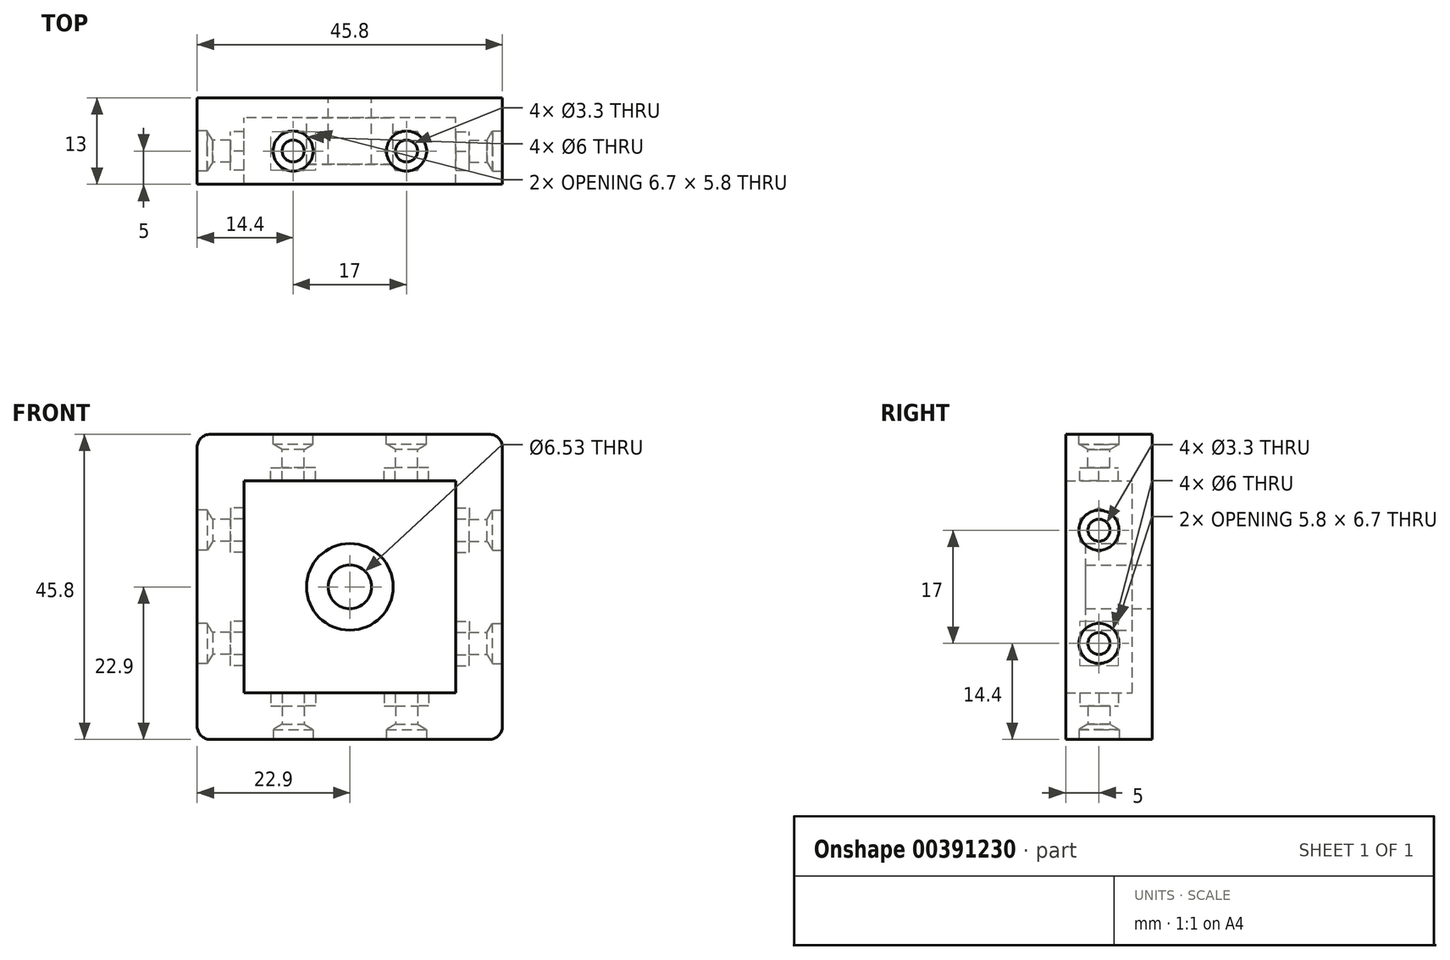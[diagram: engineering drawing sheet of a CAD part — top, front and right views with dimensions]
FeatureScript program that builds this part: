
annotation { "Feature Type Name" : "Feature", "Feature Type Description" : "" }
export const myFeature = defineFeature(function(context is Context, id is Id, definition is map)
    precondition{}
    {
        {
            var Q0;
            Q0=qCreatedBy(makeId("Front.planeOp"),FACE);
            var sketch = newSketch(context, id + "F0", { "sketchPlane" : qUnion([Q0])});
            skLineSegment(sketch, "E0.bottom", {"start": v(22.9, -22.9) * mm, "end": v(-22.9, -22.9) * mm});
            skLineSegment(sketch, "E0.top", {"start": v(22.9, 22.9) * mm, "end": v(-22.9, 22.9) * mm});
            skLineSegment(sketch, "E0.left", {"start": v(22.9, -22.9) * mm, "end": v(22.9, 22.9) * mm});
            skLineSegment(sketch, "E0.right", {"start": v(-22.9, -22.9) * mm, "end": v(-22.9, 22.9) * mm});
            skPoint(sketch, "E0.middle", {"position": v(0, 0) * mm});
            skLineSegment(sketch, "E1.bottom", {"start": v(15.9, -15.9) * mm, "end": v(-15.9, -15.9) * mm});
            skLineSegment(sketch, "E1.top", {"start": v(15.9, 15.9) * mm, "end": v(-15.9, 15.9) * mm});
            skLineSegment(sketch, "E1.left", {"start": v(15.9, -15.9) * mm, "end": v(15.9, 15.9) * mm});
            skLineSegment(sketch, "E1.right", {"start": v(-15.9, -15.9) * mm, "end": v(-15.9, 15.9) * mm});
            skCircle(sketch, "E2", {"center": v(0, 0) * mm, "radius": 6.5 * mm});
            skSolve(sketch);
        }
        {
            var Q0;
            Q0=makeQuery(id+"F0.imprint","IMPRINT",FACE,{"disambiguationData":[TD([[makeQuery(id+"F0.imprint","IMPRINT",EDGE,{"derivedFrom":sQuery(id+"F0.wireOp",EDGE,"E1.bottom")}),-1.0]])]});
            extrude(context, id + "F1", {"entities" : qUnion([Q0]), "depth" : 3 * mm});
        }
        {
            var Q0;
            Q0=makeQuery(id+"F0.imprint","IMPRINT",FACE,{"disambiguationData":[TD([[makeQuery(id+"F0.imprint","IMPRINT",EDGE,{"derivedFrom":sQuery(id+"F0.wireOp",EDGE,"E2")}),1.0]])]});
            extrude(context, id + "F2", {"entities" : qUnion([Q0]), "operationType" : NewBodyOperationType.ADD, "depth" : 10 * mm});
        }
        {
            var Q0;
            Q0=makeQuery(id+"F0.imprint","IMPRINT",FACE,{"disambiguationData":[TD([[makeQuery(id+"F0.imprint","IMPRINT",EDGE,{"derivedFrom":sQuery(id+"F0.wireOp",EDGE,"E0.bottom")}),-1.0]])]});
            extrude(context, id + "F3", {"entities" : qUnion([Q0]), "operationType" : NewBodyOperationType.ADD, "depth" : 13 * mm});
        }
        {
            var Q0;
            Q0=makeQuery(id+"F3.opExtrude","SWEPT_FACE",FACE,{"disambiguationData":[OSD([sQuery(id+"F0.wireOp",EDGE,"E0.bottom")])]});
            var sketch = newSketch(context, id + "F4", { "sketchPlane" : qUnion([Q0])});
            skPoint(sketch, "E3", {"position": v(-8.5, 8) * mm});
            skPoint(sketch, "E4", {"position": v(8.5, 8) * mm});
            skCircle(sketch, "E5.cCircle", {"center": v(-8.5, 8) * mm, "radius": 2.9 * mm, "construction": true});
            skLineSegment(sketch, "E5.0", {"start": v(-5.15, 8) * mm, "end": v(-6.83, 5.1) * mm});
            skLineSegment(sketch, "E5.1", {"start": v(-6.83, 5.1) * mm, "end": v(-10.17, 5.1) * mm});
            skLineSegment(sketch, "E5.2", {"start": v(-10.17, 5.1) * mm, "end": v(-11.85, 8) * mm});
            skLineSegment(sketch, "E5.3", {"start": v(-11.85, 8) * mm, "end": v(-10.17, 10.9) * mm});
            skLineSegment(sketch, "E5.4", {"start": v(-10.17, 10.9) * mm, "end": v(-6.83, 10.9) * mm});
            skLineSegment(sketch, "E5.5", {"start": v(-6.83, 10.9) * mm, "end": v(-5.15, 8) * mm});
            skPoint(sketch, "E5.0.midPoint", {"position": v(-5.99, 6.55) * mm});
            skCircle(sketch, "E6.cCircle", {"center": v(8.5, 8) * mm, "radius": 2.9 * mm, "construction": true});
            skLineSegment(sketch, "E6.0", {"start": v(11.85, 8) * mm, "end": v(10.17, 5.1) * mm});
            skLineSegment(sketch, "E6.1", {"start": v(10.17, 5.1) * mm, "end": v(6.83, 5.1) * mm});
            skLineSegment(sketch, "E6.2", {"start": v(6.83, 5.1) * mm, "end": v(5.15, 8) * mm});
            skLineSegment(sketch, "E6.3", {"start": v(5.15, 8) * mm, "end": v(6.83, 10.9) * mm});
            skLineSegment(sketch, "E6.4", {"start": v(6.83, 10.9) * mm, "end": v(10.17, 10.9) * mm});
            skLineSegment(sketch, "E6.5", {"start": v(10.17, 10.9) * mm, "end": v(11.85, 8) * mm});
            skPoint(sketch, "E6.0.midPoint", {"position": v(11.01, 6.55) * mm});
            skSolve(sketch);
        }
        {
            var Q0;
            Q0=makeQuery(id+"F4.imprint","IMPRINT",FACE,{"disambiguationData":[TD([[makeQuery(id+"F4.imprint","IMPRINT",EDGE,{"derivedFrom":sQuery(id+"F4.wireOp",EDGE,"E5.0")}),-1.0]])]});
            var Q1;
            Q1=makeQuery(id+"F4.imprint","IMPRINT",FACE,{"disambiguationData":[TD([[makeQuery(id+"F4.imprint","IMPRINT",EDGE,{"derivedFrom":sQuery(id+"F4.wireOp",EDGE,"E6.0")}),-1.0]])]});
            extrude(context, id + "F5", {"entities" : qUnion([Q0, Q1]), "operationType" : NewBodyOperationType.REMOVE, "oppositeDirection" : true, "depth" : 8 * mm, "hasSecondDirection" : true, "secondDirectionOppositeDirection" : true, "secondDirectionDepth" : 5 * mm});
        }
        {
            var Q0;
            Q0=sQuery(id+"F4.wireOp",VERTEX,"E3");
            var Q1;
            Q1=sQuery(id+"F4.wireOp",VERTEX,"E4");
            var Q2;
            Q2=makeQuery(id+"F1.opExtrude","SWEPT_BODY",BODY,{"disambiguationData":[OSD([sQuery(id+"F0.wireOp",EDGE,"E1.bottom"),sQuery(id+"F0.wireOp",EDGE,"E1.top"),sQuery(id+"F0.wireOp",EDGE,"E1.left"),sQuery(id+"F0.wireOp",EDGE,"E1.right"),sQuery(id+"F0.wireOp",EDGE,"E2")])]});
            hole(context, id + "F6", {"style" : HoleStyle.SIMPLE, "endStyle" : HoleEndStyle.BLIND, "holeDiameter" : 6 * mm, "holeDepth" : 1.5 * mm, "tappedDepth" : 12 * mm, "tapClearance" : 3, "locations" : qUnion([Q0, Q1]), "scope" : qUnion([Q2])});
        }
        {
            var Q0;
            Q0=sQuery(id+"F4.wireOp",VERTEX,"E3");
            var Q1;
            Q1=sQuery(id+"F4.wireOp",VERTEX,"E4");
            var Q2;
            Q2=makeQuery(id+"F1.opExtrude","SWEPT_BODY",BODY,{"disambiguationData":[OSD([sQuery(id+"F0.wireOp",EDGE,"E1.bottom"),sQuery(id+"F0.wireOp",EDGE,"E1.top"),sQuery(id+"F0.wireOp",EDGE,"E1.left"),sQuery(id+"F0.wireOp",EDGE,"E1.right"),sQuery(id+"F0.wireOp",EDGE,"E2")])]});
            hole(context, id + "F7", {"style" : HoleStyle.SIMPLE, "endStyle" : HoleEndStyle.BLIND, "standardTappedOrClearance" : lookupTablePath({ "standard" : "ISO", "fit" : "Normal", "size" : "M3", "type" : "Clearance" }), "standardBlindInLast" : lookupTablePath({ "fit" : "Standard", "standard" : "ISO", "size" : "M3", "type" : "Clearance" }), "holeDiameter" : 3.3 * mm, "holeDepth" : 10 * mm, "tappedDepth" : 12 * mm, "tapClearance" : 3, "locations" : qUnion([Q0, Q1]), "scope" : qUnion([Q2])});
        }
        {
            var Q0;
            Q0=makeQuery(id+"F3.opExtrude","SWEPT_FACE",FACE,{"disambiguationData":[OSD([sQuery(id+"F0.wireOp",EDGE,"E0.left")])]});
            var sketch = newSketch(context, id + "F8", { "sketchPlane" : qUnion([Q0])});
            skPoint(sketch, "E7", {"position": v(-8, -8.5) * mm});
            skPoint(sketch, "E8", {"position": v(-8, 8.5) * mm});
            skCircle(sketch, "E9.cCircle", {"center": v(-8, -8.5) * mm, "radius": 2.9 * mm, "construction": true});
            skLineSegment(sketch, "E9.0", {"start": v(-8, -5.15) * mm, "end": v(-5.1, -6.83) * mm});
            skLineSegment(sketch, "E9.1", {"start": v(-5.1, -6.83) * mm, "end": v(-5.1, -10.17) * mm});
            skLineSegment(sketch, "E9.2", {"start": v(-5.1, -10.17) * mm, "end": v(-8, -11.85) * mm});
            skLineSegment(sketch, "E9.3", {"start": v(-8, -11.85) * mm, "end": v(-10.9, -10.17) * mm});
            skLineSegment(sketch, "E9.4", {"start": v(-10.9, -10.17) * mm, "end": v(-10.9, -6.83) * mm});
            skLineSegment(sketch, "E9.5", {"start": v(-10.9, -6.83) * mm, "end": v(-8, -5.15) * mm});
            skPoint(sketch, "E9.0.midPoint", {"position": v(-6.55, -5.99) * mm});
            skCircle(sketch, "E10.cCircle", {"center": v(-8, 8.5) * mm, "radius": 2.9 * mm, "construction": true});
            skLineSegment(sketch, "E10.0", {"start": v(-8, 11.85) * mm, "end": v(-5.1, 10.17) * mm});
            skLineSegment(sketch, "E10.1", {"start": v(-5.1, 10.17) * mm, "end": v(-5.1, 6.83) * mm});
            skLineSegment(sketch, "E10.2", {"start": v(-5.1, 6.83) * mm, "end": v(-8, 5.15) * mm});
            skLineSegment(sketch, "E10.3", {"start": v(-8, 5.15) * mm, "end": v(-10.9, 6.83) * mm});
            skLineSegment(sketch, "E10.4", {"start": v(-10.9, 6.83) * mm, "end": v(-10.9, 10.17) * mm});
            skLineSegment(sketch, "E10.5", {"start": v(-10.9, 10.17) * mm, "end": v(-8, 11.85) * mm});
            skPoint(sketch, "E10.0.midPoint", {"position": v(-6.55, 11.01) * mm});
            skSolve(sketch);
        }
        {
            var Q0;
            Q0=qSketchRegion(id+"F8",true);
            extrude(context, id + "F9", {"entities" : qUnion([Q0]), "operationType" : NewBodyOperationType.REMOVE, "oppositeDirection" : true, "depth" : 8 * mm, "hasSecondDirection" : true, "secondDirectionOppositeDirection" : true, "secondDirectionDepth" : 5 * mm});
        }
        {
            var Q0;
            Q0=makeQuery(id+"F3.opExtrude","SWEPT_FACE",FACE,{"disambiguationData":[OSD([sQuery(id+"F0.wireOp",EDGE,"E0.top")])]});
            var sketch = newSketch(context, id + "F10", { "sketchPlane" : qUnion([Q0])});
            skPoint(sketch, "E11", {"position": v(8.5, -8) * mm});
            skPoint(sketch, "E12", {"position": v(-8.5, -8) * mm});
            skCircle(sketch, "E13.cCircle", {"center": v(8.5, -8) * mm, "radius": 2.9 * mm, "construction": true});
            skLineSegment(sketch, "E13.0", {"start": v(5.15, -8) * mm, "end": v(6.83, -5.1) * mm});
            skLineSegment(sketch, "E13.1", {"start": v(6.83, -5.1) * mm, "end": v(10.17, -5.1) * mm});
            skLineSegment(sketch, "E13.2", {"start": v(10.17, -5.1) * mm, "end": v(11.85, -8) * mm});
            skLineSegment(sketch, "E13.3", {"start": v(11.85, -8) * mm, "end": v(10.17, -10.9) * mm});
            skLineSegment(sketch, "E13.4", {"start": v(10.17, -10.9) * mm, "end": v(6.83, -10.9) * mm});
            skLineSegment(sketch, "E13.5", {"start": v(6.83, -10.9) * mm, "end": v(5.15, -8) * mm});
            skPoint(sketch, "E13.0.midPoint", {"position": v(5.99, -6.55) * mm});
            skCircle(sketch, "E14.cCircle", {"center": v(-8.5, -8) * mm, "radius": 2.9 * mm, "construction": true});
            skLineSegment(sketch, "E14.0", {"start": v(-10.17, -5.1) * mm, "end": v(-6.83, -5.1) * mm});
            skLineSegment(sketch, "E14.1", {"start": v(-6.83, -5.1) * mm, "end": v(-5.15, -8) * mm});
            skLineSegment(sketch, "E14.2", {"start": v(-5.15, -8) * mm, "end": v(-6.83, -10.9) * mm});
            skLineSegment(sketch, "E14.3", {"start": v(-6.83, -10.9) * mm, "end": v(-10.17, -10.9) * mm});
            skLineSegment(sketch, "E14.4", {"start": v(-10.17, -10.9) * mm, "end": v(-11.85, -8) * mm});
            skLineSegment(sketch, "E14.5", {"start": v(-11.85, -8) * mm, "end": v(-10.17, -5.1) * mm});
            skPoint(sketch, "E14.0.midPoint", {"position": v(-8.5, -5.1) * mm});
            skSolve(sketch);
        }
        {
            var Q0;
            Q0=qSketchRegion(id+"F10",true);
            extrude(context, id + "F11", {"entities" : qUnion([Q0]), "operationType" : NewBodyOperationType.REMOVE, "oppositeDirection" : true, "depth" : 8 * mm, "hasSecondDirection" : true, "secondDirectionOppositeDirection" : true, "secondDirectionDepth" : 5 * mm});
        }
        {
            var Q0;
            Q0=sQuery(id+"F10.wireOp",VERTEX,"E11");
            var Q1;
            Q1=sQuery(id+"F10.wireOp",VERTEX,"E12");
            var Q2;
            Q2=makeQuery(id+"F1.opExtrude","SWEPT_BODY",BODY,{"disambiguationData":[OSD([sQuery(id+"F0.wireOp",EDGE,"E1.bottom"),sQuery(id+"F0.wireOp",EDGE,"E1.top"),sQuery(id+"F0.wireOp",EDGE,"E1.left"),sQuery(id+"F0.wireOp",EDGE,"E1.right"),sQuery(id+"F0.wireOp",EDGE,"E2")])]});
            hole(context, id + "F12", {"style" : HoleStyle.SIMPLE, "endStyle" : HoleEndStyle.BLIND, "standardTappedOrClearance" : lookupTablePath({ "standard" : "ISO", "fit" : "Normal", "size" : "M3", "type" : "Clearance" }), "standardBlindInLast" : lookupTablePath({ "fit" : "Standard", "standard" : "ISO", "size" : "M3", "type" : "Clearance" }), "holeDiameter" : 3.3 * mm, "holeDepth" : 10 * mm, "tappedDepth" : 12 * mm, "tapClearance" : 3, "locations" : qUnion([Q0, Q1]), "scope" : qUnion([Q2])});
        }
        {
            var Q0;
            Q0=sQuery(id+"F10.wireOp",VERTEX,"E11");
            var Q1;
            Q1=sQuery(id+"F10.wireOp",VERTEX,"E12");
            var Q2;
            Q2=makeQuery(id+"F1.opExtrude","SWEPT_BODY",BODY,{"disambiguationData":[OSD([sQuery(id+"F0.wireOp",EDGE,"E1.bottom"),sQuery(id+"F0.wireOp",EDGE,"E1.top"),sQuery(id+"F0.wireOp",EDGE,"E1.left"),sQuery(id+"F0.wireOp",EDGE,"E1.right"),sQuery(id+"F0.wireOp",EDGE,"E2")])]});
            hole(context, id + "F13", {"style" : HoleStyle.SIMPLE, "endStyle" : HoleEndStyle.BLIND, "holeDiameter" : 6 * mm, "holeDepth" : 1.5 * mm, "tappedDepth" : 12 * mm, "tapClearance" : 3, "locations" : qUnion([Q0, Q1]), "scope" : qUnion([Q2])});
        }
        {
            var Q0;
            Q0=sQuery(id+"F8.wireOp",VERTEX,"E7");
            var Q1;
            Q1=sQuery(id+"F8.wireOp",VERTEX,"E8");
            var Q2;
            Q2=makeQuery(id+"F1.opExtrude","SWEPT_BODY",BODY,{"disambiguationData":[OSD([sQuery(id+"F0.wireOp",EDGE,"E1.bottom"),sQuery(id+"F0.wireOp",EDGE,"E1.top"),sQuery(id+"F0.wireOp",EDGE,"E1.left"),sQuery(id+"F0.wireOp",EDGE,"E1.right"),sQuery(id+"F0.wireOp",EDGE,"E2")])]});
            hole(context, id + "F14", {"style" : HoleStyle.SIMPLE, "endStyle" : HoleEndStyle.BLIND, "holeDiameter" : 6 * mm, "holeDepth" : 1.5 * mm, "tappedDepth" : 12 * mm, "tapClearance" : 3, "locations" : qUnion([Q0, Q1]), "scope" : qUnion([Q2])});
        }
        {
            var Q0;
            Q0=sQuery(id+"F8.wireOp",VERTEX,"E7");
            var Q1;
            Q1=sQuery(id+"F8.wireOp",VERTEX,"E8");
            var Q2;
            Q2=makeQuery(id+"F1.opExtrude","SWEPT_BODY",BODY,{"disambiguationData":[OSD([sQuery(id+"F0.wireOp",EDGE,"E1.bottom"),sQuery(id+"F0.wireOp",EDGE,"E1.top"),sQuery(id+"F0.wireOp",EDGE,"E1.left"),sQuery(id+"F0.wireOp",EDGE,"E1.right"),sQuery(id+"F0.wireOp",EDGE,"E2")])]});
            hole(context, id + "F15", {"style" : HoleStyle.SIMPLE, "endStyle" : HoleEndStyle.BLIND, "standardTappedOrClearance" : lookupTablePath({ "standard" : "ISO", "fit" : "Normal", "size" : "M3", "type" : "Clearance" }), "standardBlindInLast" : lookupTablePath({ "fit" : "Standard", "standard" : "ISO", "size" : "M3", "type" : "Clearance" }), "holeDiameter" : 3.3 * mm, "holeDepth" : 10 * mm, "tappedDepth" : 12 * mm, "tapClearance" : 3, "locations" : qUnion([Q0, Q1]), "scope" : qUnion([Q2])});
        }
        {
            var Q0;
            Q0=makeQuery(id+"F3.opExtrude","SWEPT_FACE",FACE,{"disambiguationData":[OSD([sQuery(id+"F0.wireOp",EDGE,"E0.right")])]});
            var sketch = newSketch(context, id + "F16", { "sketchPlane" : qUnion([Q0])});
            skPoint(sketch, "E15", {"position": v(8, 8.5) * mm});
            skPoint(sketch, "E16", {"position": v(8, -8.5) * mm});
            skCircle(sketch, "E17.cCircle", {"center": v(8, 8.5) * mm, "radius": 2.9 * mm, "construction": true});
            skLineSegment(sketch, "E17.0", {"start": v(5.1, 6.83) * mm, "end": v(5.1, 10.17) * mm});
            skLineSegment(sketch, "E17.1", {"start": v(5.1, 10.17) * mm, "end": v(8, 11.85) * mm});
            skLineSegment(sketch, "E17.2", {"start": v(8, 11.85) * mm, "end": v(10.9, 10.17) * mm});
            skLineSegment(sketch, "E17.3", {"start": v(10.9, 10.17) * mm, "end": v(10.9, 6.83) * mm});
            skLineSegment(sketch, "E17.4", {"start": v(10.9, 6.83) * mm, "end": v(8, 5.15) * mm});
            skLineSegment(sketch, "E17.5", {"start": v(8, 5.15) * mm, "end": v(5.1, 6.83) * mm});
            skPoint(sketch, "E17.0.midPoint", {"position": v(5.1, 8.5) * mm});
            skCircle(sketch, "E18.cCircle", {"center": v(8, -8.5) * mm, "radius": 2.9 * mm, "construction": true});
            skLineSegment(sketch, "E18.0", {"start": v(5.1, -10.17) * mm, "end": v(5.1, -6.83) * mm});
            skLineSegment(sketch, "E18.1", {"start": v(5.1, -6.83) * mm, "end": v(8, -5.15) * mm});
            skLineSegment(sketch, "E18.2", {"start": v(8, -5.15) * mm, "end": v(10.9, -6.83) * mm});
            skLineSegment(sketch, "E18.3", {"start": v(10.9, -6.83) * mm, "end": v(10.9, -10.17) * mm});
            skLineSegment(sketch, "E18.4", {"start": v(10.9, -10.17) * mm, "end": v(8, -11.85) * mm});
            skLineSegment(sketch, "E18.5", {"start": v(8, -11.85) * mm, "end": v(5.1, -10.17) * mm});
            skPoint(sketch, "E18.0.midPoint", {"position": v(5.1, -8.5) * mm});
            skSolve(sketch);
        }
        {
            var Q0;
            Q0=qSketchRegion(id+"F16",true);
            extrude(context, id + "F17", {"entities" : qUnion([Q0]), "operationType" : NewBodyOperationType.REMOVE, "oppositeDirection" : true, "depth" : 8 * mm, "hasSecondDirection" : true, "secondDirectionOppositeDirection" : true, "secondDirectionDepth" : 5 * mm});
        }
        {
            var Q0;
            Q0=sQuery(id+"F16.wireOp",VERTEX,"E15");
            var Q1;
            Q1=sQuery(id+"F16.wireOp",VERTEX,"E16");
            var Q2;
            Q2=makeQuery(id+"F1.opExtrude","SWEPT_BODY",BODY,{"disambiguationData":[OSD([sQuery(id+"F0.wireOp",EDGE,"E1.bottom"),sQuery(id+"F0.wireOp",EDGE,"E1.top"),sQuery(id+"F0.wireOp",EDGE,"E1.left"),sQuery(id+"F0.wireOp",EDGE,"E1.right"),sQuery(id+"F0.wireOp",EDGE,"E2")])]});
            hole(context, id + "F18", {"style" : HoleStyle.SIMPLE, "endStyle" : HoleEndStyle.BLIND, "standardTappedOrClearance" : lookupTablePath({ "standard" : "ISO", "fit" : "Normal", "size" : "M3", "type" : "Clearance" }), "standardBlindInLast" : lookupTablePath({ "fit" : "Standard", "standard" : "ISO", "size" : "M3", "type" : "Clearance" }), "holeDiameter" : 3.3 * mm, "holeDepth" : 10 * mm, "tappedDepth" : 12 * mm, "tapClearance" : 3, "locations" : qUnion([Q0, Q1]), "scope" : qUnion([Q2])});
        }
        {
            var Q0;
            Q0=sQuery(id+"F16.wireOp",VERTEX,"E15");
            var Q1;
            Q1=sQuery(id+"F16.wireOp",VERTEX,"E16");
            var Q2;
            Q2=makeQuery(id+"F1.opExtrude","SWEPT_BODY",BODY,{"disambiguationData":[OSD([sQuery(id+"F0.wireOp",EDGE,"E1.bottom"),sQuery(id+"F0.wireOp",EDGE,"E1.top"),sQuery(id+"F0.wireOp",EDGE,"E1.left"),sQuery(id+"F0.wireOp",EDGE,"E1.right"),sQuery(id+"F0.wireOp",EDGE,"E2")])]});
            hole(context, id + "F19", {"style" : HoleStyle.SIMPLE, "endStyle" : HoleEndStyle.BLIND, "holeDiameter" : 6 * mm, "holeDepth" : 1.5 * mm, "tappedDepth" : 12 * mm, "tapClearance" : 3, "locations" : qUnion([Q0, Q1]), "scope" : qUnion([Q2])});
        }
        {
            var Q0;
            Q0=makeQuery(id+"F3.opExtrude","SWEPT_EDGE",EDGE,{"disambiguationData":[OSD([sQuery(id+"F0.wireOp",EDGE,"E0.top"),sQuery(id+"F0.wireOp",EDGE,"E0.left")])]});
            var Q1;
            Q1=makeQuery(id+"F3.opExtrude","SWEPT_EDGE",EDGE,{"disambiguationData":[OSD([sQuery(id+"F0.wireOp",EDGE,"E0.bottom"),sQuery(id+"F0.wireOp",EDGE,"E0.left")])]});
            var Q2;
            Q2=makeQuery(id+"F3.opExtrude","SWEPT_EDGE",EDGE,{"disambiguationData":[OSD([sQuery(id+"F0.wireOp",EDGE,"E0.bottom"),sQuery(id+"F0.wireOp",EDGE,"E0.right")])]});
            var Q3;
            Q3=makeQuery(id+"F3.opExtrude","SWEPT_EDGE",EDGE,{"disambiguationData":[OSD([sQuery(id+"F0.wireOp",EDGE,"E0.top"),sQuery(id+"F0.wireOp",EDGE,"E0.right")])]});
            fillet(context, id + "F20", {"entities" : qUnion([Q0, Q1, Q2, Q3]), "radius" : 2 * mm, "tangentPropagation" : true, "allowEdgeOverflow" : false});
        }
        {
            var Q0;
            Q0=sQuery(id+"F0.wireOp",VERTEX,"E0.middle");
            var Q1;
            Q1=makeQuery(id+"F1.opExtrude","SWEPT_BODY",BODY,{"disambiguationData":[OSD([sQuery(id+"F0.wireOp",EDGE,"E1.bottom"),sQuery(id+"F0.wireOp",EDGE,"E1.top"),sQuery(id+"F0.wireOp",EDGE,"E1.left"),sQuery(id+"F0.wireOp",EDGE,"E1.right"),sQuery(id+"F0.wireOp",EDGE,"E2")])]});
            hole(context, id + "F21", {"style" : HoleStyle.SIMPLE, "endStyle" : HoleEndStyle.BLIND, "oppositeDirection" : true, "standardTappedOrClearance" : lookupTablePath({ "standard" : "ANSI", "fit" : "Close", "size" : "1/4", "type" : "Clearance" }), "standardBlindInLast" : lookupTablePath({ "fit" : "Close", "standard" : "ANSI", "size" : "1/4", "type" : "Clearance" }), "holeDiameter" : 6.53 * mm, "holeDepth" : 15.8 * mm, "tappedDepth" : 12 * mm, "tapClearance" : 3, "locations" : qUnion([Q0]), "scope" : qUnion([Q1])});
        }
    });
